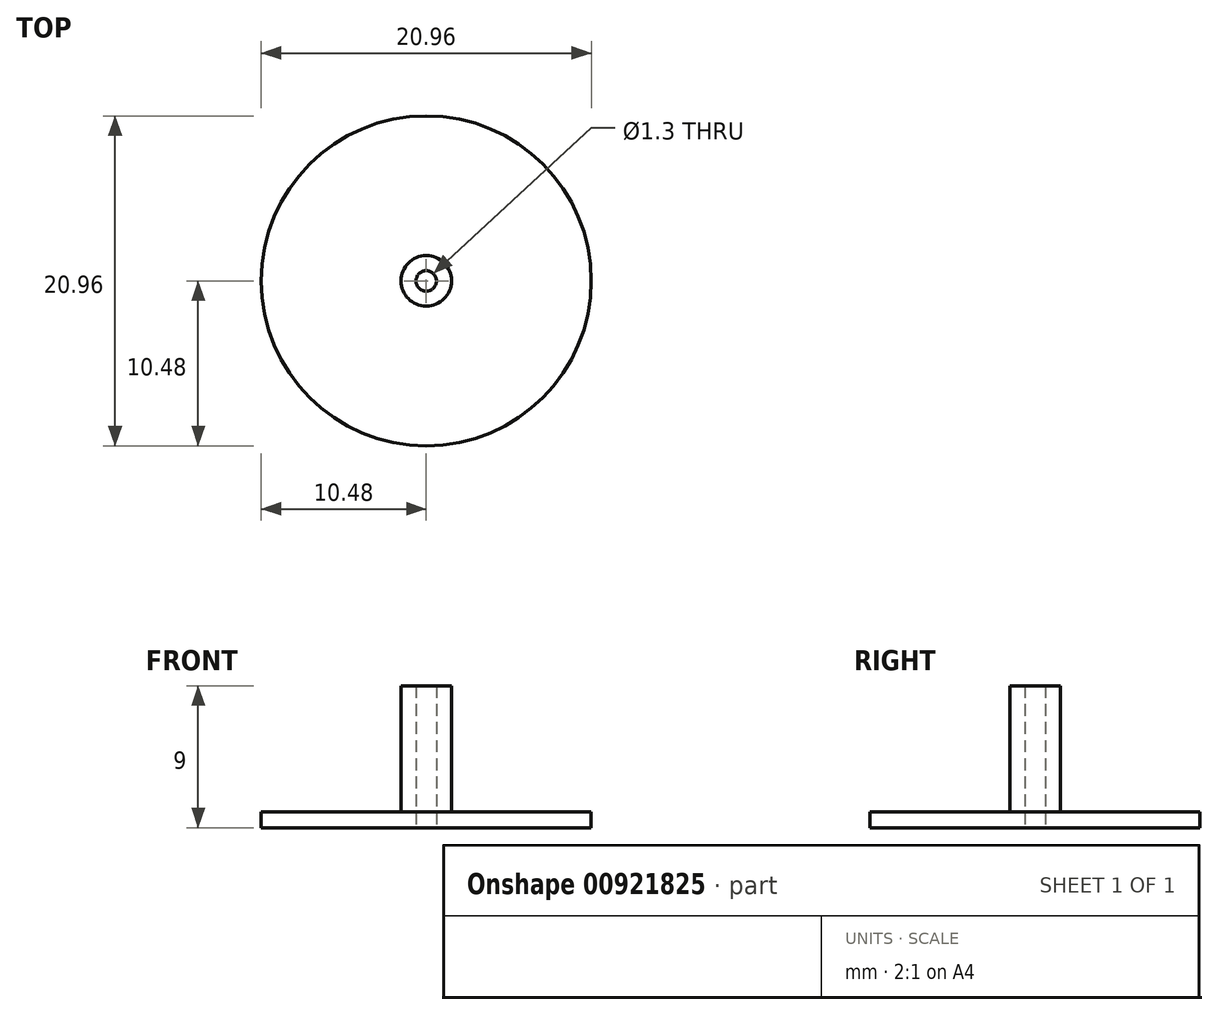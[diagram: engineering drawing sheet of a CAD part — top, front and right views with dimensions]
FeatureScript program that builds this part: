
annotation { "Feature Type Name" : "Feature", "Feature Type Description" : "" }
export const myFeature = defineFeature(function(context is Context, id is Id, definition is map)
    precondition{}
    {
        {
            var Q0;
            Q0=qCreatedBy(makeId("Top.planeOp"),FACE);
            var sketch = newSketch(context, id + "F0", { "sketchPlane" : qUnion([Q0])});
            skCircle(sketch, "E0", {"center": v(0, 0) * mm, "radius": 1.6 * mm});
            skSolve(sketch);
        }
        {
            var Q0;
            Q0=qCreatedBy(makeId("Top.planeOp"),FACE);
            var sketch = newSketch(context, id + "F1", { "sketchPlane" : qUnion([Q0])});
            skCircle(sketch, "E1", {"center": v(0, 0) * mm, "radius": 10.48 * mm});
            skSolve(sketch);
        }
        {
            var Q0;
            Q0 = qSketchRegion(id + "F1", true);
            extrude(context, id + "F2", {"entities" : qUnion([Q0]), "depth" : 1 * mm, "offsetDistance" : 25 * mm});
        }
        {
            var Q0;
            Q0 = qSketchRegion(id + "F0", true);
            extrude(context, id + "F3", {"entities" : qUnion([Q0]), "operationType" : NewBodyOperationType.ADD, "depth" : 9 * mm, "offsetDistance" : 25 * mm});
        }
        {
            var Q0;
            Q0=qCreatedBy(makeId("Top.planeOp"),FACE);
            var sketch = newSketch(context, id + "F4", { "sketchPlane" : qUnion([Q0])});
            skCircle(sketch, "E2", {"center": v(0, 0) * mm, "radius": 0.65 * mm});
            skSolve(sketch);
        }
        {
            var Q0;
            Q0 = qSketchRegion(id + "F4", true);
            extrude(context, id + "F5", {"entities" : qUnion([Q0]), "operationType" : NewBodyOperationType.REMOVE, "flatOperationType" : FlatOperationType.REMOVE, "depth" : 12.7 * mm, "offsetDistance" : 25 * mm, "domain" : OperationDomain.MODEL});
        }
    });
